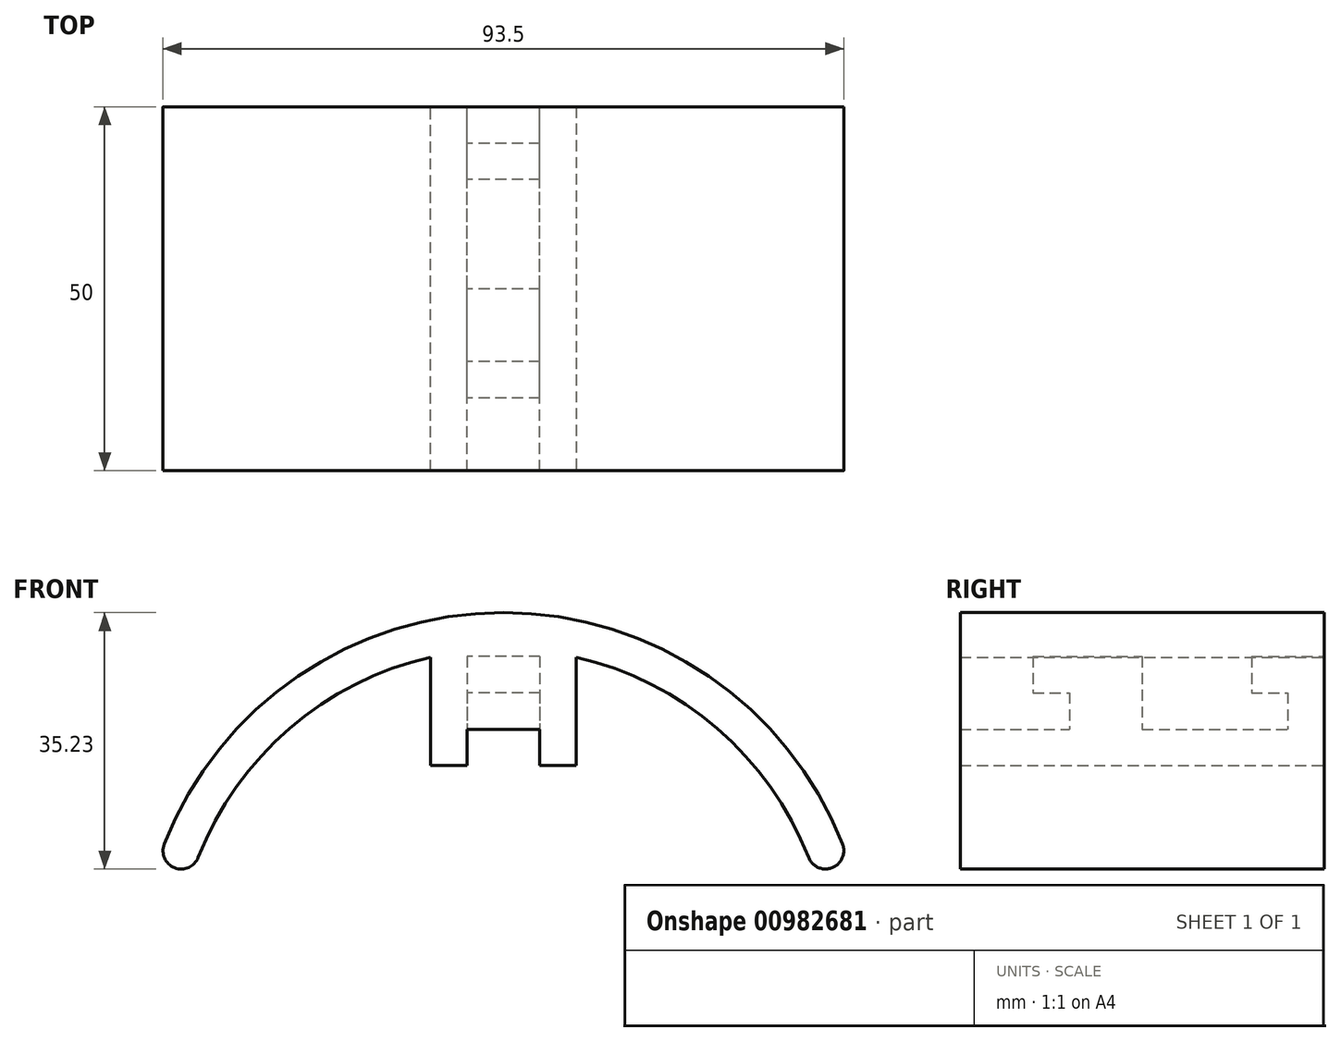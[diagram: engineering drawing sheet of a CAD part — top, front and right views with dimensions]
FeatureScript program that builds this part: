
annotation { "Feature Type Name" : "Feature", "Feature Type Description" : "" }
export const myFeature = defineFeature(function(context is Context, id is Id, definition is map)
    precondition{}
    {
        {
            var Q0;
            Q0=qCreatedBy(makeId("Right.planeOp"),FACE);
            var sketch = newSketch(context, id + "F0", { "sketchPlane" : qUnion([Q0])});
            skLineSegment(sketch, "E0.top", {"start": v(0, 0) * mm, "end": v(50, 0) * mm});
            skLineSegment(sketch, "E0.right", {"start": v(50, -20) * mm, "end": v(50, 0) * mm});
            skPoint(sketch, "E1", {"position": v(0, -20) * mm});
            skLineSegment(sketch, "E2", {"start": v(50, -20) * mm, "end": v(0, -20) * mm});
            skLineSegment(sketch, "E3", {"start": v(0, -20) * mm, "end": v(0, 0) * mm});
            skSolve(sketch);
        }
        {
            var Q0;
            Q0 = qSketchRegion(id + "F0", true);
            extrude(context, id + "F1", {"entities" : qUnion([Q0]), "depth" : 20 * mm, "offsetDistance" : 25.4 * mm});
        }
        {
            var Q0;
            Q0=makeQuery(id+"F1.opExtrude","SWEPT_FACE",FACE,{"disambiguationData":[OSD([sQuery(id+"F0.wireOp",EDGE,"E0.right")])]});
            cPlane(context, id + "F2", {"entities" : qUnion([Q0]), "cplaneType" : CPlaneType.OFFSET, "offset" : 0 * mm, "width" : 152.4 * mm, "height" : 152.4 * mm});
        }
        {
            var Q0;
            Q0=qCreatedBy(id+"F2.planeOp",FACE);
            var sketch = newSketch(context, id + "F3", { "sketchPlane" : qUnion([Q0])});
            skArc(sketch, "E4", {"start": v(36.58, -30.8) * mm, "mid": v(-10, 1.01) * mm, "end": v(-56.58, -30.8) * mm});
            skArc(sketch, "E5", {"start": v(31.92, -32.62) * mm, "mid": v(-10, -3.99) * mm, "end": v(-51.92, -32.62) * mm});
            skLineSegment(sketch, "E6", {"start": v(-10, -48.99) * mm, "end": v(-51.92, -32.62) * mm, "construction": true});
            skLineSegment(sketch, "E7", {"start": v(-10, -48.99) * mm, "end": v(31.92, -32.62) * mm, "construction": true});
            skLineSegment(sketch, "E8", {"start": v(31.92, -32.62) * mm, "end": v(-69.72, -32.62) * mm, "construction": true});
            skArc(sketch, "E9", {"start": v(-56.58, -30.8) * mm, "mid": v(-55.16, -34.04) * mm, "end": v(-51.92, -32.62) * mm});
            skArc(sketch, "E10", {"start": v(31.92, -32.62) * mm, "mid": v(35.16, -34.04) * mm, "end": v(36.58, -30.8) * mm});
            skSolve(sketch);
        }
        {
            var Q0;
            Q0 = qSketchRegion(id + "F3", true);
            extrude(context, id + "F4", {"entities" : qUnion([Q0]), "operationType" : NewBodyOperationType.ADD, "oppositeDirection" : true, "depth" : 50 * mm, "offsetDistance" : 25.4 * mm});
        }
        {
            var Q0;
            Q0=qCreatedBy(id+"F2.planeOp",FACE);
            var sketch = newSketch(context, id + "F5", { "sketchPlane" : qUnion([Q0])});
            skLineSegment(sketch, "E11.bottom", {"start": v(-15, -5) * mm, "end": v(-5, -5) * mm});
            skLineSegment(sketch, "E11.top", {"start": v(-15, -15) * mm, "end": v(-5, -15) * mm});
            skLineSegment(sketch, "E11.left", {"start": v(-15, -5) * mm, "end": v(-15, -15) * mm});
            skLineSegment(sketch, "E11.right", {"start": v(-5, -5) * mm, "end": v(-5, -15) * mm});
            skSolve(sketch);
        }
        {
            var Q0;
            Q0 = qSketchRegion(id + "F5", true);
            extrude(context, id + "F6", {"entities" : qUnion([Q0]), "operationType" : NewBodyOperationType.REMOVE, "oppositeDirection" : true, "depth" : 5 * mm, "offsetDistance" : 25.4 * mm});
        }
        {
            var Q0;
            Q0=qCreatedBy(id+"F2.planeOp",FACE);
            var sketch = newSketch(context, id + "F7", { "sketchPlane" : qUnion([Q0])});
            skLineSegment(sketch, "E12.bottom", {"start": v(-15, -5) * mm, "end": v(-5, -5) * mm});
            skLineSegment(sketch, "E12.top", {"start": v(-15, -10) * mm, "end": v(-5, -10) * mm});
            skLineSegment(sketch, "E12.left", {"start": v(-15, -5) * mm, "end": v(-15, -10) * mm});
            skLineSegment(sketch, "E12.right", {"start": v(-5, -5) * mm, "end": v(-5, -10) * mm});
            skSolve(sketch);
        }
        {
            var Q0;
            Q0 = qSketchRegion(id + "F7", true);
            extrude(context, id + "F8", {"entities" : qUnion([Q0]), "operationType" : NewBodyOperationType.REMOVE, "oppositeDirection" : true, "depth" : 10 * mm, "offsetDistance" : 25.4 * mm});
        }
        {
            var Q0;
            Q0=qCreatedBy(id+"F2.planeOp",FACE);
            var sketch = newSketch(context, id + "F9", { "sketchPlane" : qUnion([Q0])});
            skLineSegment(sketch, "E13.bottom", {"start": v(-15, -15) * mm, "end": v(-5, -15) * mm});
            skLineSegment(sketch, "E13.top", {"start": v(-15, -20) * mm, "end": v(-5, -20) * mm});
            skLineSegment(sketch, "E13.left", {"start": v(-15, -15) * mm, "end": v(-15, -20) * mm});
            skLineSegment(sketch, "E13.right", {"start": v(-5, -15) * mm, "end": v(-5, -20) * mm});
            skSolve(sketch);
        }
        {
            var Q0;
            Q0 = qSketchRegion(id + "F9", true);
            extrude(context, id + "F10", {"entities" : qUnion([Q0]), "operationType" : NewBodyOperationType.REMOVE, "oppositeDirection" : true, "depth" : 50 * mm, "offsetDistance" : 25.4 * mm});
        }
        {
            var Q0;
            Q0=makeQuery(id+"F4.boolean.opBoolean","MERGE",FACE,{"derivedFrom":[makeQuery(id+"F1.opExtrude","SWEPT_FACE",FACE,{"disambiguationData":[OSD([sQuery(id+"F0.wireOp",EDGE,"E0.right")])]}),makeQuery(id+"F4.opExtrude","CAP_FACE",FACE,{"disambiguationData":[OSD([sQuery(id+"F3.wireOp",EDGE,"E4"),sQuery(id+"F3.wireOp",EDGE,"E5"),sQuery(id+"F3.wireOp",EDGE,"E9"),sQuery(id+"F3.wireOp",EDGE,"E10")])],"isStart":true})]});
            cPlane(context, id + "F11", {"entities" : qUnion([Q0]), "cplaneType" : CPlaneType.OFFSET, "offset" : 30 * mm, "oppositeDirection" : true, "width" : 152.4 * mm, "height" : 152.4 * mm});
        }
        {
            var Q0;
            Q0=qCreatedBy(id+"F11.planeOp",FACE);
            var sketch = newSketch(context, id + "F12", { "sketchPlane" : qUnion([Q0])});
            skLineSegment(sketch, "E14.bottom", {"start": v(-15, -5) * mm, "end": v(-5, -5) * mm});
            skLineSegment(sketch, "E14.top", {"start": v(-15, -10) * mm, "end": v(-5, -10) * mm});
            skLineSegment(sketch, "E14.left", {"start": v(-15, -5) * mm, "end": v(-15, -10) * mm});
            skLineSegment(sketch, "E14.right", {"start": v(-5, -5) * mm, "end": v(-5, -10) * mm});
            skSolve(sketch);
        }
        {
            var Q0;
            Q0 = qSketchRegion(id + "F12", true);
            extrude(context, id + "F13", {"entities" : qUnion([Q0]), "operationType" : NewBodyOperationType.REMOVE, "oppositeDirection" : true, "depth" : 10 * mm, "offsetDistance" : 25.4 * mm});
        }
        {
            var Q0;
            Q0=qCreatedBy(id+"F11.planeOp",FACE);
            var sketch = newSketch(context, id + "F14", { "sketchPlane" : qUnion([Q0])});
            skLineSegment(sketch, "E15.bottom", {"start": v(-15, -5) * mm, "end": v(-5, -5) * mm});
            skLineSegment(sketch, "E15.top", {"start": v(-15, -15) * mm, "end": v(-5, -15) * mm});
            skLineSegment(sketch, "E15.left", {"start": v(-15, -5) * mm, "end": v(-15, -15) * mm});
            skLineSegment(sketch, "E15.right", {"start": v(-5, -5) * mm, "end": v(-5, -15) * mm});
            skSolve(sketch);
        }
        {
            var Q0;
            Q0 = qSketchRegion(id + "F14", true);
            extrude(context, id + "F15", {"entities" : qUnion([Q0]), "operationType" : NewBodyOperationType.REMOVE, "oppositeDirection" : true, "depth" : 5 * mm, "offsetDistance" : 25.4 * mm});
        }
        {
            var Q0;
            Q0=qCreatedBy(id+"F11.planeOp",FACE);
            var sketch = newSketch(context, id + "F16", { "sketchPlane" : qUnion([Q0])});
            skLineSegment(sketch, "E16.bottom", {"start": v(-15, -5) * mm, "end": v(-5, -5) * mm});
            skLineSegment(sketch, "E16.top", {"start": v(-15, -15) * mm, "end": v(-5, -15) * mm});
            skLineSegment(sketch, "E16.left", {"start": v(-15, -5) * mm, "end": v(-15, -15) * mm});
            skLineSegment(sketch, "E16.right", {"start": v(-5, -5) * mm, "end": v(-5, -15) * mm});
            skSolve(sketch);
        }
        {
            var Q0;
            Q0 = qSketchRegion(id + "F16", true);
            extrude(context, id + "F17", {"entities" : qUnion([Q0]), "operationType" : NewBodyOperationType.REMOVE, "depth" : 5 * mm, "offsetDistance" : 25.4 * mm});
        }
    });
